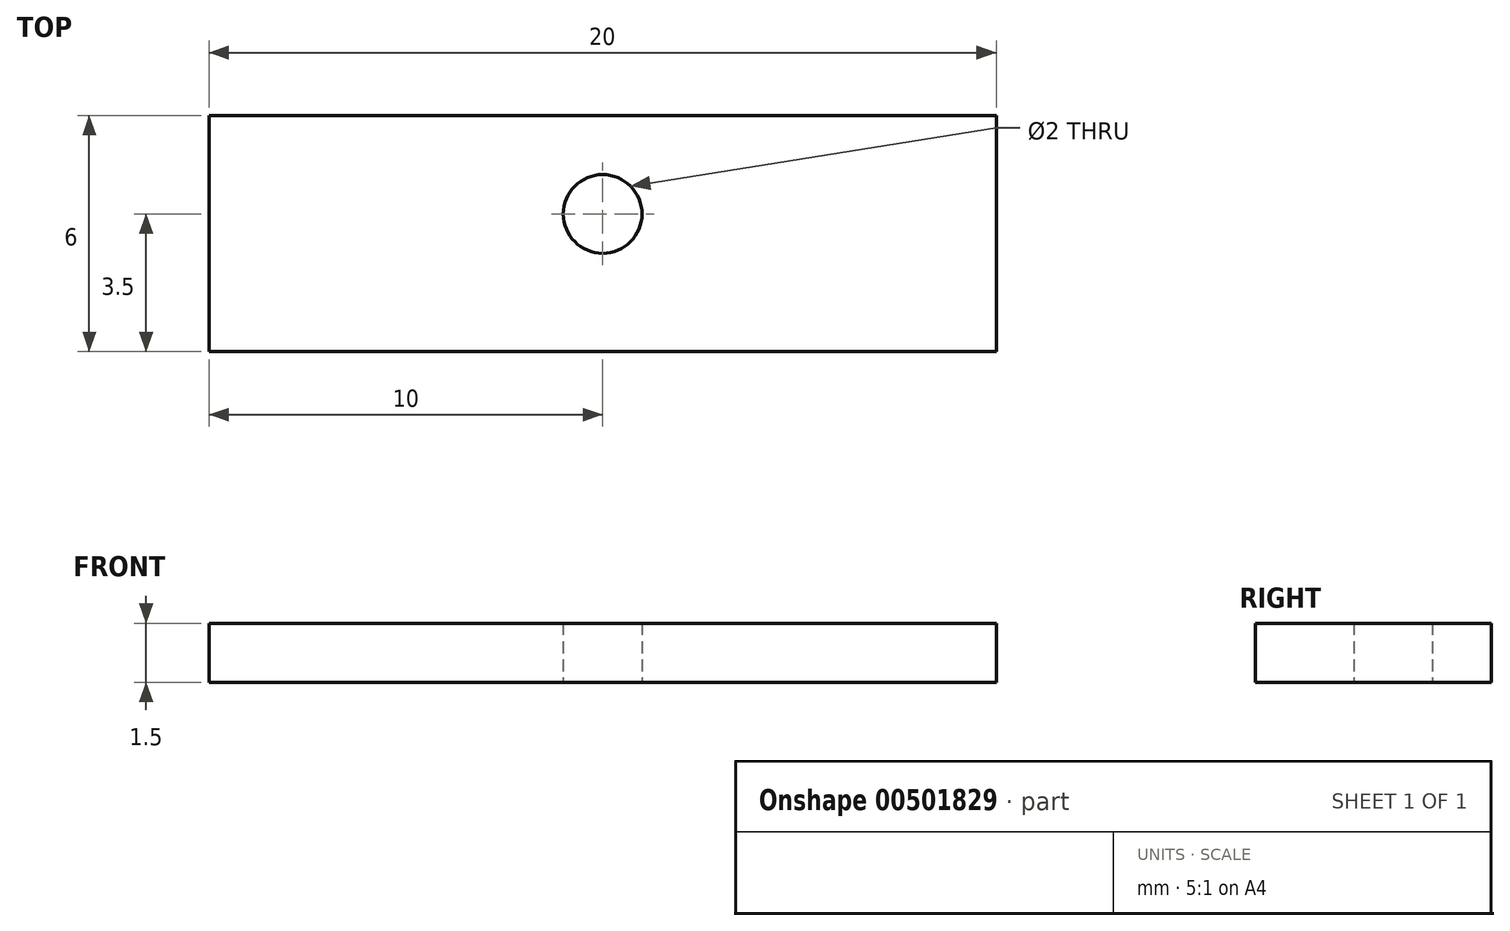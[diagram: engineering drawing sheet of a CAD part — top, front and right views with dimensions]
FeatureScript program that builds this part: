
annotation { "Feature Type Name" : "Feature", "Feature Type Description" : "" }
export const myFeature = defineFeature(function(context is Context, id is Id, definition is map)
    precondition{}
    {
        {
            var Q0;
            Q0=qCreatedBy(makeId("Top.planeOp"),FACE);
            var sketch = newSketch(context, id + "F0", { "sketchPlane" : qUnion([Q0])});
            skLineSegment(sketch, "E0.bottom", {"start": v(-10, 2) * mm, "end": v(10, 2) * mm});
            skLineSegment(sketch, "E0.top", {"start": v(-10, -4) * mm, "end": v(10, -4) * mm});
            skLineSegment(sketch, "E0.left", {"start": v(-10, 2) * mm, "end": v(-10, -4) * mm});
            skLineSegment(sketch, "E0.right", {"start": v(10, 2) * mm, "end": v(10, -4) * mm});
            skCircle(sketch, "E1", {"center": v(0, -0.5) * mm, "radius": 1 * mm});
            skSolve(sketch);
        }
        {
            var Q0;
            Q0 = qSketchRegion(id + "F0", true);
            extrude(context, id + "F1", {"entities" : qUnion([Q0]), "depth" : 1.5 * mm});
        }
    });
